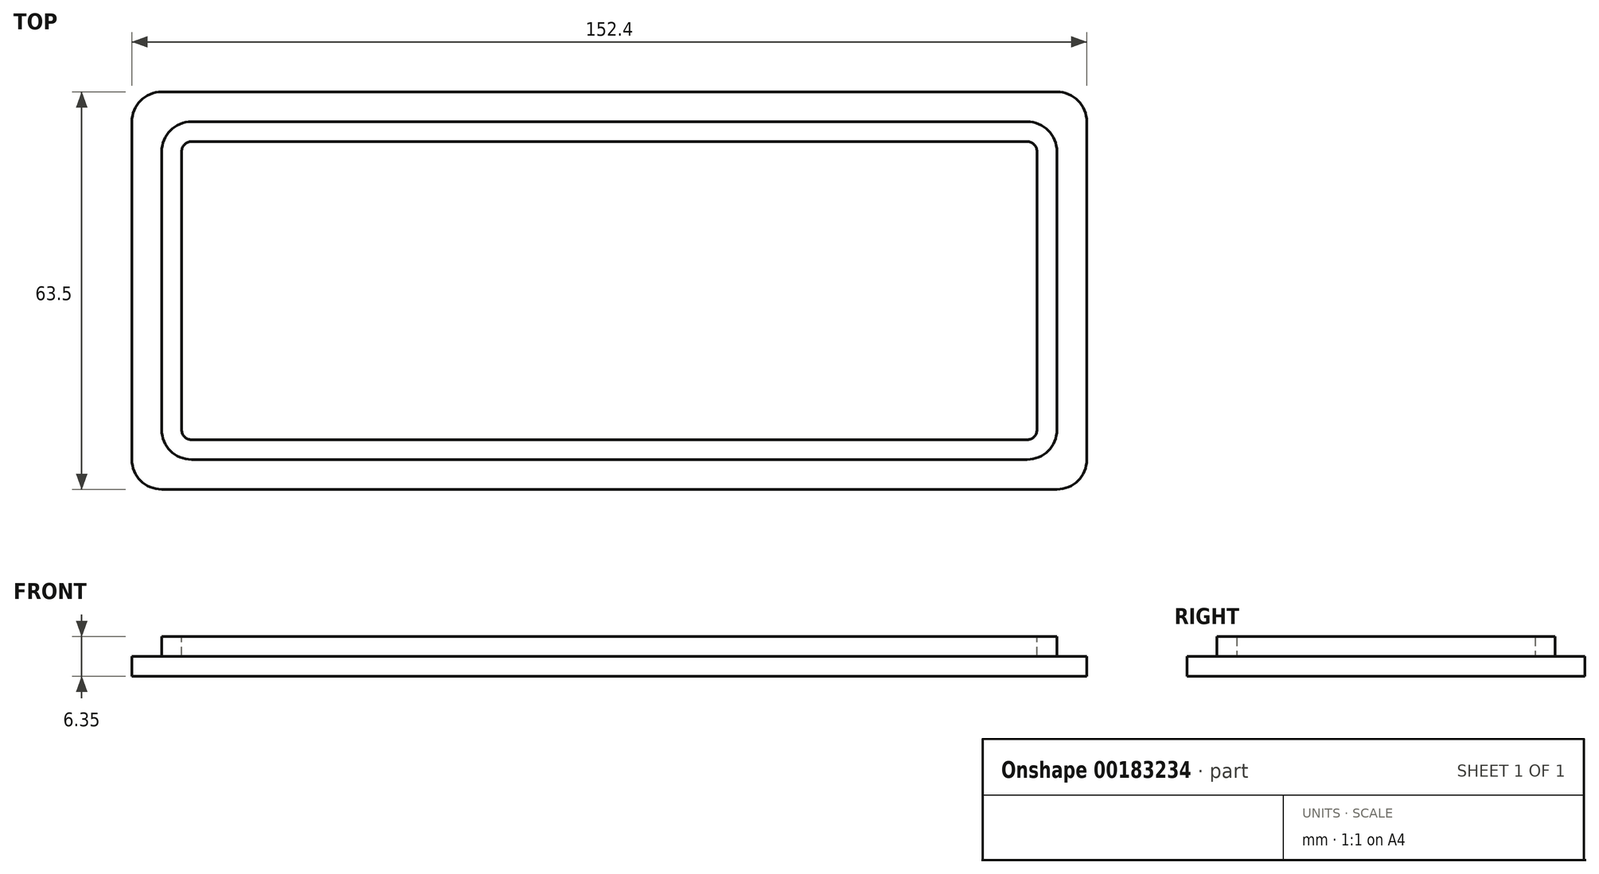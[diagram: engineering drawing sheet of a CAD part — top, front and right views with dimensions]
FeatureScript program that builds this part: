
annotation { "Feature Type Name" : "Feature", "Feature Type Description" : "" }
export const myFeature = defineFeature(function(context is Context, id is Id, definition is map)
    precondition{}
    {
        {
            var Q0;
            Q0=qCreatedBy(makeId("Top.planeOp"),FACE);
            var sketch = newSketch(context, id + "F0", { "sketchPlane" : qUnion([Q0])});
            skLineSegment(sketch, "E0.bottom", {"start": v(76.2, -31.75) * mm, "end": v(-76.2, -31.75) * mm});
            skLineSegment(sketch, "E0.top", {"start": v(76.2, 31.75) * mm, "end": v(-76.2, 31.75) * mm});
            skLineSegment(sketch, "E0.left", {"start": v(76.2, -31.75) * mm, "end": v(76.2, 31.75) * mm});
            skLineSegment(sketch, "E0.right", {"start": v(-76.2, -31.75) * mm, "end": v(-76.2, 31.75) * mm});
            skPoint(sketch, "E0.middle", {"position": v(0, 0) * mm});
            skSolve(sketch);
        }
        {
            var Q0;
            Q0=makeQuery(id+"F0.imprint","IMPRINT",FACE,{"disambiguationData":[TD([[makeQuery(id+"F0.imprint","IMPRINT",EDGE,{"derivedFrom":sQuery(id+"F0.wireOp",EDGE,"E0.bottom")}),-1.0]])]});
            extrude(context, id + "F1", {"entities" : qUnion([Q0]), "depth" : 3.17 * mm});
        }
        {
            var Q0;
            Q0=makeQuery(id+"F1.opExtrude","CAP_FACE",FACE,{"disambiguationData":[OSD([sQuery(id+"F0.wireOp",EDGE,"E0.bottom"),sQuery(id+"F0.wireOp",EDGE,"E0.top"),sQuery(id+"F0.wireOp",EDGE,"E0.left"),sQuery(id+"F0.wireOp",EDGE,"E0.right")])],"isStart":false});
            var sketch = newSketch(context, id + "F2", { "sketchPlane" : qUnion([Q0])});
            skLineSegment(sketch, "E1.bottom", {"start": v(71.44, -26.99) * mm, "end": v(-71.44, -26.99) * mm});
            skLineSegment(sketch, "E1.top", {"start": v(71.44, 26.99) * mm, "end": v(-71.44, 26.99) * mm});
            skLineSegment(sketch, "E1.left", {"start": v(71.44, -26.99) * mm, "end": v(71.44, 26.99) * mm});
            skLineSegment(sketch, "E1.right", {"start": v(-71.44, -26.99) * mm, "end": v(-71.44, 26.99) * mm});
            skPoint(sketch, "E1.middle", {"position": v(0, 0) * mm});
            skSolve(sketch);
        }
        {
            var Q0;
            Q0=makeQuery(id+"F2.imprint","IMPRINT",FACE,{"disambiguationData":[TD([[makeQuery(id+"F2.imprint","IMPRINT",EDGE,{"derivedFrom":sQuery(id+"F2.wireOp",EDGE,"E1.bottom")}),-1.0]])]});
            extrude(context, id + "F3", {"entities" : qUnion([Q0]), "operationType" : NewBodyOperationType.ADD, "depth" : 3.17 * mm});
        }
        {
            var Q0;
            Q0=makeQuery(id+"F3.opExtrude","SWEPT_EDGE",EDGE,{"disambiguationData":[OSD([sQuery(id+"F2.wireOp",EDGE,"E1.bottom"),sQuery(id+"F2.wireOp",EDGE,"E1.left")])]});
            var Q1;
            Q1=makeQuery(id+"F3.opExtrude","SWEPT_EDGE",EDGE,{"disambiguationData":[OSD([sQuery(id+"F2.wireOp",EDGE,"E1.top"),sQuery(id+"F2.wireOp",EDGE,"E1.left")])]});
            var Q2;
            Q2=makeQuery(id+"F3.opExtrude","SWEPT_EDGE",EDGE,{"disambiguationData":[OSD([sQuery(id+"F2.wireOp",EDGE,"E1.bottom"),sQuery(id+"F2.wireOp",EDGE,"E1.right")])]});
            var Q3;
            Q3=makeQuery(id+"F1.opExtrude","SWEPT_EDGE",EDGE,{"disambiguationData":[OSD([sQuery(id+"F0.wireOp",EDGE,"E0.bottom"),sQuery(id+"F0.wireOp",EDGE,"E0.left")])]});
            var Q4;
            Q4=makeQuery(id+"F1.opExtrude","SWEPT_EDGE",EDGE,{"disambiguationData":[OSD([sQuery(id+"F0.wireOp",EDGE,"E0.top"),sQuery(id+"F0.wireOp",EDGE,"E0.left")])]});
            var Q5;
            Q5=makeQuery(id+"F1.opExtrude","SWEPT_EDGE",EDGE,{"disambiguationData":[OSD([sQuery(id+"F0.wireOp",EDGE,"E0.bottom"),sQuery(id+"F0.wireOp",EDGE,"E0.right")])]});
            var Q6;
            Q6=makeQuery(id+"F3.opExtrude","SWEPT_EDGE",EDGE,{"disambiguationData":[OSD([sQuery(id+"F2.wireOp",EDGE,"E1.top"),sQuery(id+"F2.wireOp",EDGE,"E1.right")])]});
            var Q7;
            Q7=makeQuery(id+"F1.opExtrude","SWEPT_EDGE",EDGE,{"disambiguationData":[OSD([sQuery(id+"F0.wireOp",EDGE,"E0.top"),sQuery(id+"F0.wireOp",EDGE,"E0.right")])]});
            fillet(context, id + "F4", {"entities" : qUnion([Q0, Q1, Q2, Q3, Q4, Q5, Q6, Q7]), "radius" : 4.76 * mm, "tangentPropagation" : true, "allowEdgeOverflow" : false});
        }
        {
            var Q0;
            Q0=makeQuery(id+"F3.opExtrude","CAP_FACE",FACE,{"disambiguationData":[OSD([sQuery(id+"F2.wireOp",EDGE,"E1.bottom"),sQuery(id+"F2.wireOp",EDGE,"E1.top"),sQuery(id+"F2.wireOp",EDGE,"E1.left"),sQuery(id+"F2.wireOp",EDGE,"E1.right")])],"isStart":false});
            shell(context, id + "F5", {"entities" : qUnion([Q0]), "thickness" : 3.17 * mm});
        }
    });
